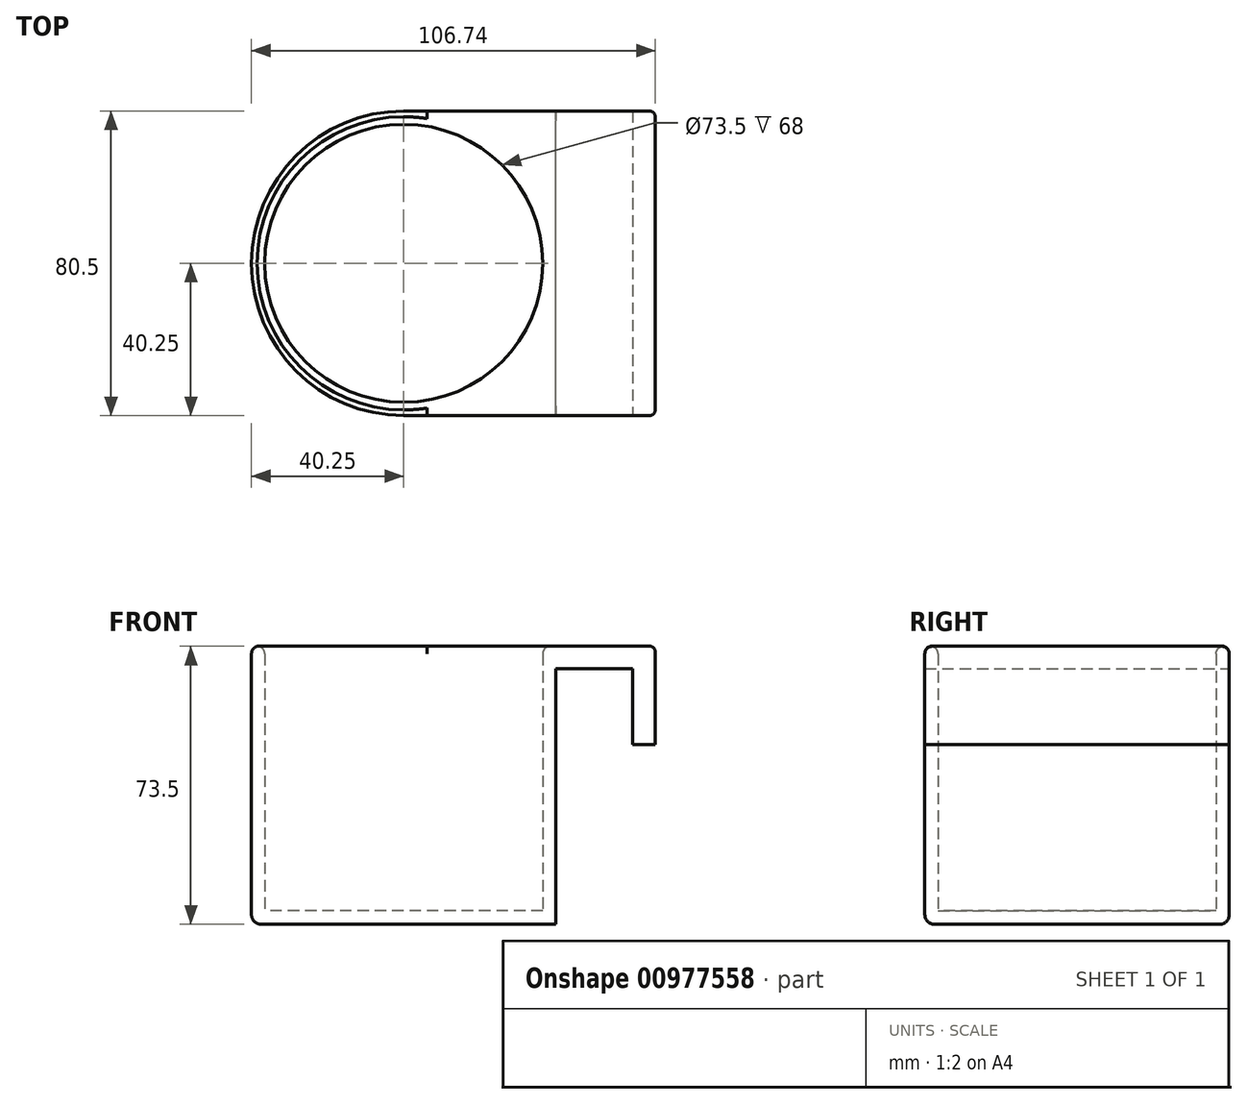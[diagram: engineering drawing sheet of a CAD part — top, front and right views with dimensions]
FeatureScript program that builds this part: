
annotation { "Feature Type Name" : "Feature", "Feature Type Description" : "" }
export const myFeature = defineFeature(function(context is Context, id is Id, definition is map)
    precondition{}
    {
        {
            var Q0;
            Q0=qCreatedBy(makeId("Top.planeOp"),FACE);
            var sketch = newSketch(context, id + "F0", { "sketchPlane" : qUnion([Q0])});
            skCircle(sketch, "E0", {"center": v(0, 0) * mm, "radius": 36.75 * mm});
            skCircle(sketch, "E1.0", {"center": v(0, 0) * mm, "radius": 40.25 * mm});
            skLineSegment(sketch, "E2", {"start": v(0, 40.25) * mm, "end": v(0, -40.25) * mm});
            skLineSegment(sketch, "E3", {"start": v(40.25, 0) * mm, "end": v(40.25, -40.25) * mm});
            skLineSegment(sketch, "E4", {"start": v(40.25, 0) * mm, "end": v(40.25, 40.25) * mm});
            skLineSegment(sketch, "E5", {"start": v(40.25, -40.25) * mm, "end": v(0, -40.25) * mm});
            skLineSegment(sketch, "E6", {"start": v(40.25, 40.25) * mm, "end": v(0, 40.25) * mm});
            skSolve(sketch);
        }
        {
            var Q0;
            {var subQ0=sQuery(id+"F0.wireOp",EDGE,"E0");var subQ2=makeQuery(id+"F0.imprint","INTERSECT",VERTEX,{"derivedFrom":[subQ0,sQuery(id+"F0.wireOp",EDGE,"qNfax2wb-XtXg-i7Pk-iPPv-2wHZnRwCyRtR")]});Q0=makeQuery(id+"F0.imprint","IMPRINT",FACE,{"disambiguationData":[TD([[makeQuery(id+"F0.imprint","IMPRINT",EDGE,{"disambiguationData":[TD([[subQ2,-1.0]])],"derivedFrom":subQ0}),1.0]])]});}
            extrude(context, id + "F1", {"entities" : qUnion([Q0]), "depth" : 70 * mm, "offsetDistance" : 25 * mm});
        }
        {
            var Q0;
            Q0=makeQuery(id+"F1.opExtrude","CAP_FACE",FACE,{"disambiguationData":[OSD([sQuery(id+"F0.wireOp",EDGE,"E0")])],"isStart":false});
            shell(context, id + "F2", {"entities" : qUnion([Q0]), "thickness" : 3.5 * mm, "oppositeDirection" : true});
        }
        {
            var Q0;
            {var subQ2=sQuery(id+"F0.wireOp",EDGE,"E4");Q0=makeQuery(id+"F0.imprint","IMPRINT",FACE,{"disambiguationData":[TD([[makeQuery(id+"F0.imprint","IMPRINT",EDGE,{"derivedFrom":subQ2}),1.0]])]});}
            var Q1;
            {var subQ2=sQuery(id+"F0.wireOp",EDGE,"E3");Q1=makeQuery(id+"F0.imprint","IMPRINT",FACE,{"disambiguationData":[TD([[makeQuery(id+"F0.imprint","IMPRINT",EDGE,{"derivedFrom":subQ2}),-1.0]])]});}
            extrude(context, id + "F3", {"entities" : qUnion([Q0, Q1]), "operationType" : NewBodyOperationType.ADD, "depth" : 70 * mm, "offsetDistance" : 25 * mm});
        }
        {
            var Q0;
            {var subQ2=sQuery(id+"F0.wireOp",EDGE,"E3");Q0=makeQuery(id+"F0.imprint","IMPRINT",FACE,{"disambiguationData":[TD([[makeQuery(id+"F0.imprint","IMPRINT",EDGE,{"derivedFrom":subQ2}),-1.0]])]});}
            var Q1;
            {var subQ2=sQuery(id+"F0.wireOp",EDGE,"E4");Q1=makeQuery(id+"F0.imprint","IMPRINT",FACE,{"disambiguationData":[TD([[makeQuery(id+"F0.imprint","IMPRINT",EDGE,{"derivedFrom":subQ2}),1.0]])]});}
            extrude(context, id + "F4", {"entities" : qUnion([Q0, Q1]), "operationType" : NewBodyOperationType.ADD, "oppositeDirection" : true, "depth" : 3.5 * mm, "offsetDistance" : 25 * mm});
        }
        {
            var Q0;
            {var subQ0=sQuery(id+"F0.wireOp",EDGE,"E4");var subQ1=sQuery(id+"F0.wireOp",EDGE,"E3");Q0=makeQuery(id+"F4.boolean.opBoolean","MERGE",FACE,{"derivedFrom":[makeQuery(id+"F3.boolean.opBoolean","MERGE",FACE,{"derivedFrom":[makeQuery(id+"F3.opExtrude","SWEPT_FACE",FACE,{"disambiguationData":[OSD([subQ1])]}),makeQuery(id+"F3.opExtrude","SWEPT_FACE",FACE,{"disambiguationData":[OSD([subQ0])]})]}),makeQuery(id+"F4.opExtrude","SWEPT_FACE",FACE,{"disambiguationData":[OSD([subQ1])]}),makeQuery(id+"F4.opExtrude","SWEPT_FACE",FACE,{"disambiguationData":[OSD([subQ0])]})]});}
            var sketch = newSketch(context, id + "F5", { "sketchPlane" : qUnion([Q0])});
            skLineSegment(sketch, "E7.bottom", {"start": v(-40.25, 70) * mm, "end": v(40.25, 70) * mm});
            skLineSegment(sketch, "E7.top", {"start": v(-40.25, 64) * mm, "end": v(40.25, 64) * mm});
            skLineSegment(sketch, "E7.left", {"start": v(-40.25, 70) * mm, "end": v(-40.25, 64) * mm});
            skLineSegment(sketch, "E7.right", {"start": v(40.25, 70) * mm, "end": v(40.25, 64) * mm});
            skSolve(sketch);
        }
        {
            var Q0;
            Q0 = qSketchRegion(id + "F5", true);
            extrude(context, id + "F6", {"entities" : qUnion([Q0]), "operationType" : NewBodyOperationType.ADD, "depth" : 20.24 * mm, "offsetDistance" : 25 * mm});
        }
        {
            var Q0;
            Q0=makeQuery(id+"F6.opExtrude","CAP_FACE",FACE,{"disambiguationData":[OSD([sQuery(id+"F5.wireOp",EDGE,"E7.bottom"),sQuery(id+"F5.wireOp",EDGE,"E7.top"),sQuery(id+"F5.wireOp",EDGE,"E7.left"),sQuery(id+"F5.wireOp",EDGE,"E7.right")])],"isStart":false});
            extrude(context, id + "F7", {"entities" : qUnion([Q0]), "operationType" : NewBodyOperationType.ADD, "depth" : 6 * mm, "offsetDistance" : 25 * mm});
        }
        {
            var Q0;
            {var subQ0=sQuery(id+"F5.wireOp",EDGE,"E7.top");Q0=makeQuery(id+"F7.boolean.opBoolean","MERGE",FACE,{"derivedFrom":[makeQuery(id+"F6.opExtrude","SWEPT_FACE",FACE,{"disambiguationData":[OSD([subQ0])]}),makeQuery(id+"F7.opExtrude","SWEPT_FACE",FACE,{"disambiguationData":[OSD([subQ0])]})]});}
            var sketch = newSketch(context, id + "F8", { "sketchPlane" : qUnion([Q0])});
            skLineSegment(sketch, "E8.bottom", {"start": v(66.5, -40.25) * mm, "end": v(60.5, -40.25) * mm});
            skLineSegment(sketch, "E8.top", {"start": v(66.5, 40.25) * mm, "end": v(60.49, 40.25) * mm});
            skLineSegment(sketch, "E8.left", {"start": v(66.5, -40.25) * mm, "end": v(66.5, 40.25) * mm});
            skLineSegment(sketch, "E8.right", {"start": v(60.5, -40.25) * mm, "end": v(60.49, 40.25) * mm});
            skSolve(sketch);
        }
        {
            var Q0;
            Q0=makeQuery(id+"F8.imprint","IMPRINT",FACE,{"disambiguationData":[TD([[makeQuery(id+"F8.imprint","IMPRINT",EDGE,{"derivedFrom":sQuery(id+"F8.wireOp",EDGE,"E8.bottom")}),-1.0]])]});
            extrude(context, id + "F9", {"entities" : qUnion([Q0]), "operationType" : NewBodyOperationType.ADD, "depth" : 20 * mm, "offsetDistance" : 25 * mm});
        }
        {
            var Q0;
            {var subQ0=sQuery(id+"F0.wireOp",EDGE,"E0");Q0=makeQuery(id+"F2.opShell","OFFSET_EDGE",EDGE,{"disambiguationData":[OSD([subQ0]),TDD([makeQuery(id+"F1.opExtrude","CAP_EDGE",EDGE,{"disambiguationData":[OSD([subQ0])],"isStart":false})])]});}
            fillet(context, id + "F10", {"entities" : qUnion([Q0]), "radius" : 2 * mm, "tangentPropagation" : true, "allowEdgeOverflow" : false});
        }
        {
            var Q0;
            Q0=makeQuery(id+"F1.opExtrude","CAP_EDGE",EDGE,{"disambiguationData":[OSD([sQuery(id+"F0.wireOp",EDGE,"E0")])],"isStart":false});
            fillet(context, id + "F11", {"entities" : qUnion([Q0]), "radius" : 2 * mm, "tangentPropagation" : true, "allowEdgeOverflow" : false});
        }
        {
            var Q0;
            Q0=makeQuery(id+"F1.opExtrude","CAP_EDGE",EDGE,{"disambiguationData":[OSD([sQuery(id+"F0.wireOp",EDGE,"E0")])],"isStart":true});
            fillet(context, id + "F12", {"entities" : qUnion([Q0]), "radius" : 2.5 * mm, "tangentPropagation" : true, "allowEdgeOverflow" : false});
        }
        {
            var Q0;
            Q0=makeQuery(id+"F7.opExtrude","CAP_EDGE",EDGE,{"disambiguationData":[OSD([sQuery(id+"F5.wireOp",EDGE,"E7.bottom")])],"isStart":false});
            fillet(context, id + "F13", {"entities" : qUnion([Q0]), "radius" : 1.45 * mm, "tangentPropagation" : true, "allowEdgeOverflow" : false});
        }
    });
